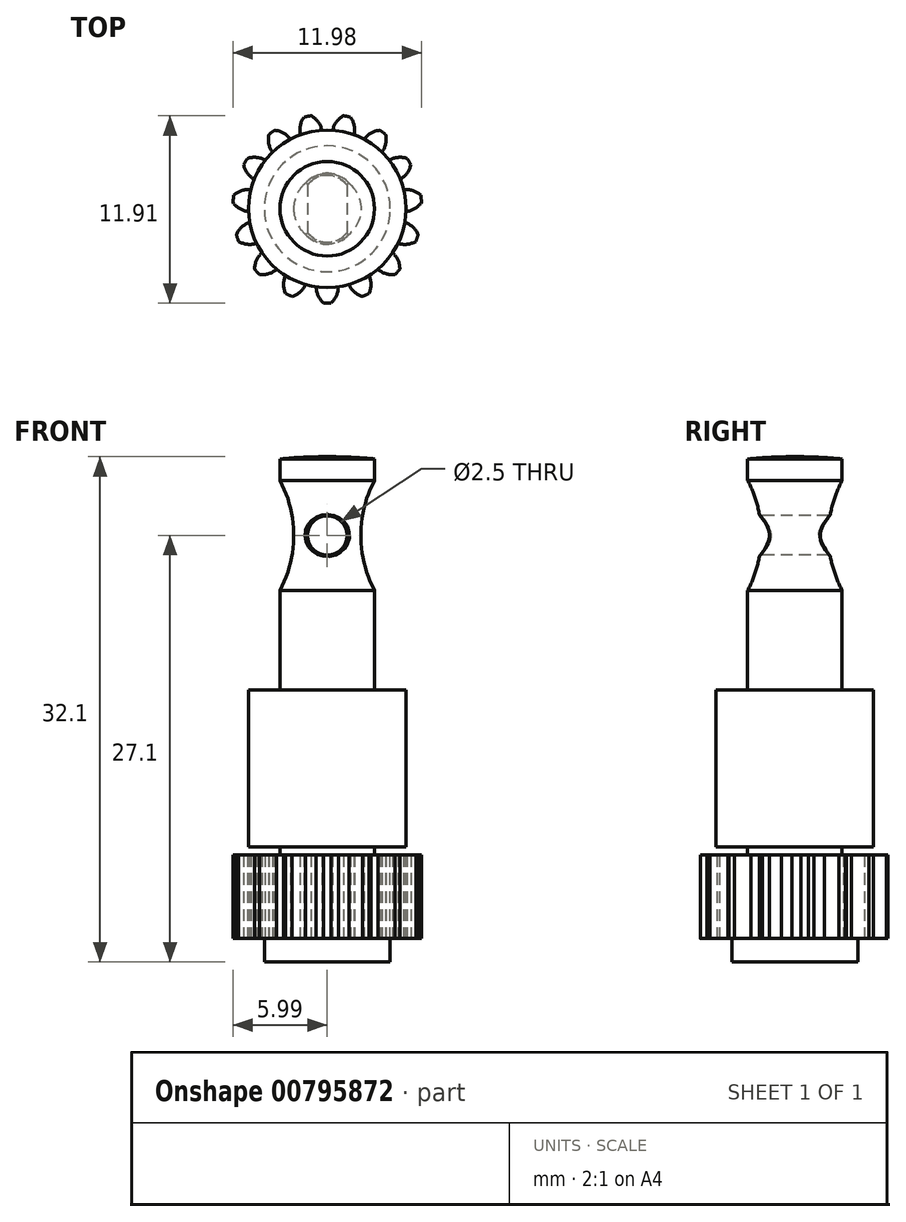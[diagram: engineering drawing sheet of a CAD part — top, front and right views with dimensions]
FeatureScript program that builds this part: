
annotation { "Feature Type Name" : "Feature", "Feature Type Description" : "" }
export const myFeature = defineFeature(function(context is Context, id is Id, definition is map)
    precondition{}
    {
        {
            assignVariable(context, id + "F0", {"name" : "H", "anyValue" : 24.8 + 7.3});
        }
        {
            var Q0;
            Q0=qCreatedBy(makeId("Top.planeOp"),FACE);
            var sketch = newSketch(context, id + "F1", { "sketchPlane" : qUnion([Q0])});
            skCircle(sketch, "E0", {"center": v(0, 0) * mm, "radius": 3 * mm});
            skSolve(sketch);
        }
        {
            var Q0;
            Q0=qSketchRegion(id+"F1",true);
            extrude(context, id + "F2", {"entities" : qUnion([Q0]), "depth" : (getVariable(context, 'H')) * mm, "offsetDistance" : 25 * mm});
        }
        {
            var Q0;
            Q0=makeQuery(id+"F2.opExtrude","CAP_FACE",FACE,{"disambiguationData":[OSD([sQuery(id+"F1.wireOp",EDGE,"E0")])],"isStart":true});
            var sketch = newSketch(context, id + "F3", { "sketchPlane" : qUnion([Q0])});
            skCircle(sketch, "E1", {"center": v(0, 0) * mm, "radius": 5 * mm});
            skCircle(sketch, "E2", {"center": v(0, 0) * mm, "radius": 3 * mm});
            skSolve(sketch);
        }
        {
            var Q0;
            Q0=qSketchRegion(id+"F3",true);
            extrude(context, id + "F4", {"entities" : qUnion([Q0]), "operationType" : NewBodyOperationType.ADD, "oppositeDirection" : true, "depth" : (getVariable(context, 'H') - 14.8) * mm, "offsetDistance" : 25 * mm, "hasSecondDirection" : true, "secondDirectionOppositeDirection" : true, "secondDirectionDepth" : 7.3 * mm});
        }
        {
            var Q0;
            Q0=makeQuery(id+"F4.boolean.opBoolean","MERGE",FACE,{"derivedFrom":[makeQuery(id+"F2.opExtrude","CAP_FACE",FACE,{"disambiguationData":[OSD([sQuery(id+"F1.wireOp",EDGE,"E0")])],"isStart":true}),makeQuery(id+"F4.opExtrude","CAP_FACE",FACE,{"disambiguationData":[OSD([sQuery(id+"F3.wireOp",EDGE,"E1")])],"isStart":true})]});
            var sketch = newSketch(context, id + "F5", { "sketchPlane" : qUnion([Q0])});
            skArc(sketch, "E3", {"start": v(-0.23, 6) * mm, "mid": v(0, 6) * mm, "end": v(0.23, 6) * mm});
            skArc(sketch, "E4", {"start": v(-0.7, 4.95) * mm, "mid": v(0, 5) * mm, "end": v(0.7, 4.95) * mm});
            skLineSegment(sketch, "E5", {"start": v(-0.7, 4.95) * mm, "end": v(0.7, 4.95) * mm, "construction": true});
            skLineSegment(sketch, "E6", {"start": v(0, 10.97) * mm, "end": v(0, 0) * mm, "construction": true});
            skArc(sketch, "E7", {"start": v(-0.7, 4.95) * mm, "mid": v(-0.58, 5.52) * mm, "end": v(-0.23, 6) * mm});
            skArc(sketch, "E8", {"start": v(0.7, 4.95) * mm, "mid": v(0.58, 5.52) * mm, "end": v(0.23, 6) * mm});
            skArc(sketch, "E9.1.0", {"start": v(-2.65, 5.38) * mm, "mid": v(-2.44, 5.48) * mm, "end": v(-2.23, 5.57) * mm});
            skArc(sketch, "E9.1.1", {"start": v(-2.65, 4.24) * mm, "mid": v(-2.77, 4.81) * mm, "end": v(-2.65, 5.38) * mm});
            skArc(sketch, "E9.1.2", {"start": v(-2.65, 4.24) * mm, "mid": v(-2.03, 4.57) * mm, "end": v(-1.37, 4.8) * mm});
            skLineSegment(sketch, "E9.1.3", {"start": v(-2.65, 4.24) * mm, "end": v(-1.37, 4.8) * mm, "construction": true});
            skArc(sketch, "E9.1.4", {"start": v(-1.37, 4.8) * mm, "mid": v(-1.72, 5.28) * mm, "end": v(-2.23, 5.57) * mm});
            skArc(sketch, "E9.2.0", {"start": v(-4.61, 3.84) * mm, "mid": v(-4.46, 4.01) * mm, "end": v(-4.3, 4.18) * mm});
            skArc(sketch, "E9.2.1", {"start": v(-4.15, 2.8) * mm, "mid": v(-4.5, 3.27) * mm, "end": v(-4.61, 3.84) * mm});
            skArc(sketch, "E9.2.2", {"start": v(-4.15, 2.8) * mm, "mid": v(-3.72, 3.35) * mm, "end": v(-3.21, 3.83) * mm});
            skLineSegment(sketch, "E9.2.3", {"start": v(-4.15, 2.8) * mm, "end": v(-3.21, 3.83) * mm, "construction": true});
            skArc(sketch, "E9.2.4", {"start": v(-3.21, 3.83) * mm, "mid": v(-3.72, 4.12) * mm, "end": v(-4.3, 4.18) * mm});
            skArc(sketch, "E10.4.3.0", {"start": v(-4.92, 0.86) * mm, "mid": v(-5.43, 1.16) * mm, "end": v(-5.77, 1.63) * mm});
            skArc(sketch, "E10.6.3.0", {"start": v(-5.77, 1.63) * mm, "mid": v(-5.7, 1.85) * mm, "end": v(-5.63, 2.07) * mm});
            skArc(sketch, "E10.8.3.0", {"start": v(-4.92, 0.86) * mm, "mid": v(-4.76, 1.55) * mm, "end": v(-4.5, 2.2) * mm});
            skLineSegment(sketch, "E10.12.3.0", {"start": v(-4.92, 0.86) * mm, "end": v(-4.5, 2.2) * mm, "construction": true});
            skArc(sketch, "E10.15.3.0", {"start": v(-4.5, 2.2) * mm, "mid": v(-5.07, 2.26) * mm, "end": v(-5.63, 2.07) * mm});
            skArc(sketch, "E10.4.4.0", {"start": v(-4.85, -1.21) * mm, "mid": v(-5.43, -1.15) * mm, "end": v(-5.94, -0.86) * mm});
            skArc(sketch, "E10.6.4.0", {"start": v(-5.94, -0.86) * mm, "mid": v(-5.97, -0.63) * mm, "end": v(-5.99, -0.4) * mm});
            skArc(sketch, "E10.8.4.0", {"start": v(-4.85, -1.21) * mm, "mid": v(-4.97, -0.52) * mm, "end": v(-5, 0.18) * mm});
            skLineSegment(sketch, "E10.12.4.0", {"start": v(-4.85, -1.21) * mm, "end": v(-5, 0.18) * mm, "construction": true});
            skArc(sketch, "E10.15.4.0", {"start": v(-5, 0.18) * mm, "mid": v(-5.55, 0) * mm, "end": v(-5.99, -0.4) * mm});
            skArc(sketch, "E10.4.5.0", {"start": v(-3.94, -3.08) * mm, "mid": v(-4.5, -3.26) * mm, "end": v(-5.08, -3.2) * mm});
            skArc(sketch, "E10.6.5.0", {"start": v(-5.08, -3.2) * mm, "mid": v(-5.2, -3) * mm, "end": v(-5.3, -2.8) * mm});
            skArc(sketch, "E10.8.5.0", {"start": v(-3.94, -3.08) * mm, "mid": v(-4.33, -2.5) * mm, "end": v(-4.64, -1.87) * mm});
            skLineSegment(sketch, "E10.12.5.0", {"start": v(-3.94, -3.08) * mm, "end": v(-4.64, -1.87) * mm, "construction": true});
            skArc(sketch, "E10.15.5.0", {"start": v(-4.64, -1.87) * mm, "mid": v(-5.07, -2.26) * mm, "end": v(-5.3, -2.8) * mm});
            skArc(sketch, "E10.4.6.0", {"start": v(-2.34, -4.42) * mm, "mid": v(-2.78, -4.8) * mm, "end": v(-3.34, -4.99) * mm});
            skArc(sketch, "E10.6.6.0", {"start": v(-3.34, -4.99) * mm, "mid": v(-3.53, -4.85) * mm, "end": v(-3.71, -4.71) * mm});
            skArc(sketch, "E10.8.6.0", {"start": v(-2.34, -4.42) * mm, "mid": v(-2.94, -4.05) * mm, "end": v(-3.48, -3.6) * mm});
            skLineSegment(sketch, "E10.12.6.0", {"start": v(-2.34, -4.42) * mm, "end": v(-3.48, -3.6) * mm, "construction": true});
            skArc(sketch, "E10.15.6.0", {"start": v(-3.48, -3.6) * mm, "mid": v(-3.71, -4.13) * mm, "end": v(-3.71, -4.71) * mm});
            skArc(sketch, "E10.4.7.0", {"start": v(-0.34, -4.99) * mm, "mid": v(-0.58, -5.52) * mm, "end": v(-1.02, -5.91) * mm});
            skArc(sketch, "E10.6.7.0", {"start": v(-1.02, -5.91) * mm, "mid": v(-1.25, -5.87) * mm, "end": v(-1.47, -5.82) * mm});
            skArc(sketch, "E10.8.7.0", {"start": v(-0.34, -4.99) * mm, "mid": v(-1.04, -4.9) * mm, "end": v(-1.71, -4.7) * mm});
            skLineSegment(sketch, "E10.12.7.0", {"start": v(-0.34, -4.99) * mm, "end": v(-1.71, -4.7) * mm, "construction": true});
            skArc(sketch, "E10.15.7.0", {"start": v(-1.71, -4.7) * mm, "mid": v(-1.71, -5.28) * mm, "end": v(-1.47, -5.82) * mm});
            skArc(sketch, "E10.4.8.0", {"start": v(1.71, -4.7) * mm, "mid": v(1.71, -5.28) * mm, "end": v(1.47, -5.82) * mm});
            skArc(sketch, "E10.6.8.0", {"start": v(1.47, -5.82) * mm, "mid": v(1.25, -5.87) * mm, "end": v(1.02, -5.91) * mm});
            skArc(sketch, "E10.8.8.0", {"start": v(1.71, -4.7) * mm, "mid": v(1.04, -4.9) * mm, "end": v(0.34, -4.99) * mm});
            skLineSegment(sketch, "E10.12.8.0", {"start": v(1.71, -4.7) * mm, "end": v(0.34, -4.99) * mm, "construction": true});
            skArc(sketch, "E10.15.8.0", {"start": v(0.34, -4.99) * mm, "mid": v(0.58, -5.52) * mm, "end": v(1.02, -5.91) * mm});
            skArc(sketch, "E10.4.9.0", {"start": v(3.48, -3.6) * mm, "mid": v(3.71, -4.13) * mm, "end": v(3.71, -4.71) * mm});
            skArc(sketch, "E10.6.9.0", {"start": v(3.71, -4.71) * mm, "mid": v(3.53, -4.85) * mm, "end": v(3.34, -4.99) * mm});
            skArc(sketch, "E10.8.9.0", {"start": v(3.48, -3.6) * mm, "mid": v(2.94, -4.05) * mm, "end": v(2.34, -4.42) * mm});
            skLineSegment(sketch, "E10.12.9.0", {"start": v(3.48, -3.6) * mm, "end": v(2.34, -4.42) * mm, "construction": true});
            skArc(sketch, "E10.15.9.0", {"start": v(2.34, -4.42) * mm, "mid": v(2.78, -4.8) * mm, "end": v(3.34, -4.99) * mm});
            skArc(sketch, "E10.4.10.0", {"start": v(4.64, -1.87) * mm, "mid": v(5.07, -2.26) * mm, "end": v(5.3, -2.8) * mm});
            skArc(sketch, "E10.6.10.0", {"start": v(5.3, -2.8) * mm, "mid": v(5.2, -3) * mm, "end": v(5.08, -3.2) * mm});
            skArc(sketch, "E10.8.10.0", {"start": v(4.64, -1.87) * mm, "mid": v(4.33, -2.5) * mm, "end": v(3.94, -3.08) * mm});
            skLineSegment(sketch, "E10.12.10.0", {"start": v(4.64, -1.87) * mm, "end": v(3.94, -3.08) * mm, "construction": true});
            skArc(sketch, "E10.15.10.0", {"start": v(3.94, -3.08) * mm, "mid": v(4.5, -3.26) * mm, "end": v(5.08, -3.2) * mm});
            skArc(sketch, "E10.4.11.0", {"start": v(5, 0.18) * mm, "mid": v(5.55, 0) * mm, "end": v(5.99, -0.4) * mm});
            skArc(sketch, "E10.6.11.0", {"start": v(5.99, -0.4) * mm, "mid": v(5.97, -0.63) * mm, "end": v(5.94, -0.86) * mm});
            skArc(sketch, "E10.8.11.0", {"start": v(5, 0.18) * mm, "mid": v(4.97, -0.52) * mm, "end": v(4.85, -1.21) * mm});
            skLineSegment(sketch, "E10.12.11.0", {"start": v(5, 0.18) * mm, "end": v(4.85, -1.21) * mm, "construction": true});
            skArc(sketch, "E10.15.11.0", {"start": v(4.85, -1.21) * mm, "mid": v(5.43, -1.15) * mm, "end": v(5.94, -0.86) * mm});
            skArc(sketch, "E11.4.12.0", {"start": v(4.5, 2.2) * mm, "mid": v(5.07, 2.26) * mm, "end": v(5.63, 2.07) * mm});
            skArc(sketch, "E11.6.12.0", {"start": v(5.63, 2.07) * mm, "mid": v(5.7, 1.85) * mm, "end": v(5.77, 1.63) * mm});
            skArc(sketch, "E11.8.12.0", {"start": v(4.5, 2.2) * mm, "mid": v(4.76, 1.55) * mm, "end": v(4.92, 0.86) * mm});
            skLineSegment(sketch, "E11.12.12.0", {"start": v(4.5, 2.2) * mm, "end": v(4.92, 0.86) * mm, "construction": true});
            skArc(sketch, "E11.15.12.0", {"start": v(4.92, 0.86) * mm, "mid": v(5.43, 1.16) * mm, "end": v(5.77, 1.63) * mm});
            skArc(sketch, "E11.4.13.0", {"start": v(3.21, 3.83) * mm, "mid": v(3.72, 4.12) * mm, "end": v(4.3, 4.18) * mm});
            skArc(sketch, "E11.6.13.0", {"start": v(4.3, 4.18) * mm, "mid": v(4.46, 4.01) * mm, "end": v(4.61, 3.84) * mm});
            skArc(sketch, "E11.8.13.0", {"start": v(3.21, 3.83) * mm, "mid": v(3.72, 3.35) * mm, "end": v(4.15, 2.8) * mm});
            skLineSegment(sketch, "E11.12.13.0", {"start": v(3.21, 3.83) * mm, "end": v(4.15, 2.8) * mm, "construction": true});
            skArc(sketch, "E11.15.13.0", {"start": v(4.15, 2.8) * mm, "mid": v(4.5, 3.27) * mm, "end": v(4.61, 3.84) * mm});
            skArc(sketch, "E12.4.14.0", {"start": v(1.37, 4.8) * mm, "mid": v(1.72, 5.28) * mm, "end": v(2.23, 5.57) * mm});
            skArc(sketch, "E12.6.14.0", {"start": v(2.23, 5.57) * mm, "mid": v(2.44, 5.48) * mm, "end": v(2.65, 5.38) * mm});
            skArc(sketch, "E12.8.14.0", {"start": v(1.37, 4.8) * mm, "mid": v(2.03, 4.57) * mm, "end": v(2.65, 4.24) * mm});
            skLineSegment(sketch, "E12.12.14.0", {"start": v(1.37, 4.8) * mm, "end": v(2.65, 4.24) * mm, "construction": true});
            skArc(sketch, "E12.15.14.0", {"start": v(2.65, 4.24) * mm, "mid": v(2.77, 4.81) * mm, "end": v(2.65, 5.38) * mm});
            skCircle(sketch, "E13", {"center": v(0, 0) * mm, "radius": 5 * mm});
            skSolve(sketch);
        }
        {
            var Q0;
            Q0=qSketchRegion(id+"F5",true);
            extrude(context, id + "F6", {"entities" : qUnion([Q0]), "operationType" : NewBodyOperationType.ADD, "oppositeDirection" : true, "depth" : 6.8 * mm, "offsetDistance" : 25 * mm});
        }
        {
            var Q0;
            Q0=qCreatedBy(makeId("Front.planeOp"),FACE);
            var sketch = newSketch(context, id + "F7", { "sketchPlane" : qUnion([Q0])});
            skLineSegment(sketch, "E14", {"start": v(0, 40.6) * mm, "end": v(0, -13.25) * mm, "construction": true});
            skArc(sketch, "E15", {"start": v(0, 32.1) * mm, "mid": v(5.06, 31.7) * mm, "end": v(10, 30.5) * mm});
            skLineSegment(sketch, "E16", {"start": v(0, 32.1) * mm, "end": v(0, 35.1) * mm});
            skLineSegment(sketch, "E17", {"start": v(0, 35.1) * mm, "end": v(10, 35.1) * mm});
            skLineSegment(sketch, "E18", {"start": v(10, 35.1) * mm, "end": v(10, 30.5) * mm});
            skSolve(sketch);
        }
        {
            var Q0;
            Q0=qSketchRegion(id+"F7",true);
            var Q1;
            Q1=sQuery(id+"F7.wireOp",EDGE,"E14");
            revolve(context, id + "F8", {"operationType" : NewBodyOperationType.REMOVE, "surfaceOperationType" : NewSurfaceOperationType.NEW, "entities" : qUnion([Q0]), "axis" : qUnion([Q1]), "revolveType" : RevolveType.FULL, "oppositeDirection" : true});
        }
        {
            var Q0;
            Q0=qCreatedBy(makeId("Front.planeOp"),FACE);
            var sketch = newSketch(context, id + "F9", { "sketchPlane" : qUnion([Q0])});
            skArc(sketch, "E19", {"start": v(3, 30.6) * mm, "mid": v(2.13, 27.1) * mm, "end": v(3, 23.6) * mm});
            skLineSegment(sketch, "E20", {"start": v(3, 30.6) * mm, "end": v(0, 30.6) * mm, "construction": true});
            skLineSegment(sketch, "E21", {"start": v(3, 23.6) * mm, "end": v(0, 23.6) * mm, "construction": true});
            skLineSegment(sketch, "E22", {"start": v(3, 0) * mm, "end": v(3, 30.6) * mm, "construction": true});
            skLineSegment(sketch, "E23", {"start": v(0, 30.6) * mm, "end": v(0, 23.6) * mm, "construction": true});
            skLineSegment(sketch, "E24", {"start": v(3, 30.6) * mm, "end": v(4.5, 30.6) * mm});
            skLineSegment(sketch, "E25", {"start": v(3, 23.6) * mm, "end": v(4.5, 23.6) * mm});
            skLineSegment(sketch, "E26", {"start": v(4.5, 23.6) * mm, "end": v(4.5, 30.6) * mm});
            skSolve(sketch);
        }
        {
            var Q0;
            Q0=qSketchRegion(id+"F9",true);
            var Q1;
            Q1=sQuery(id+"F9.wireOp",EDGE,"E23");
            revolve(context, id + "F10", {"operationType" : NewBodyOperationType.REMOVE, "surfaceOperationType" : NewSurfaceOperationType.NEW, "entities" : qUnion([Q0]), "axis" : qUnion([Q1]), "revolveType" : RevolveType.FULL, "oppositeDirection" : true});
        }
        {
            var Q0;
            Q0=qCreatedBy(makeId("Front.planeOp"),FACE);
            var sketch = newSketch(context, id + "F11", { "sketchPlane" : qUnion([Q0])});
            skCircle(sketch, "E27", {"center": v(0, 27.1) * mm, "radius": 1.25 * mm});
            skLineSegment(sketch, "E28", {"start": v(9.63, 27.1) * mm, "end": v(0, 27.1) * mm, "construction": true});
            skSolve(sketch);
        }
        {
            var Q0;
            Q0=qSketchRegion(id+"F11",true);
            extrude(context, id + "F12", {"entities" : qUnion([Q0]), "operationType" : NewBodyOperationType.REMOVE, "endBound" : BoundingType.SYMMETRIC, "oppositeDirection" : true, "depth" : 10 * mm, "offsetDistance" : 25 * mm});
        }
        {
            var Q0;
            Q0=makeQuery(id+"F12.boolean.opBoolean","INTERSECT",EDGE,{"disambiguationData":[OD(0.0)],"derivedFrom":[makeQuery(id+"F10.boolean.opBoolean","COPY",FACE,{"derivedFrom":makeQuery(id+"F10.opRevolve","SWEPT_FACE",FACE,{"disambiguationData":[OSD([sQuery(id+"F9.wireOp",EDGE,"E19")])]})}),makeQuery(id+"F12.opExtrude","SWEPT_FACE",FACE,{"disambiguationData":[OSD([sQuery(id+"F11.wireOp",EDGE,"E27")])]})]});
            fillet(context, id + "F13", {"entities" : qUnion([Q0]), "radius" : 0.1 * mm, "tangentPropagation" : true, "allowEdgeOverflow" : false});
        }
        {
            var Q0;
            Q0=makeQuery(id+"F12.boolean.opBoolean","INTERSECT",EDGE,{"disambiguationData":[OD(1.0)],"derivedFrom":[makeQuery(id+"F10.boolean.opBoolean","COPY",FACE,{"derivedFrom":makeQuery(id+"F10.opRevolve","SWEPT_FACE",FACE,{"disambiguationData":[OSD([sQuery(id+"F9.wireOp",EDGE,"E19")])]})}),makeQuery(id+"F12.opExtrude","SWEPT_FACE",FACE,{"disambiguationData":[OSD([sQuery(id+"F11.wireOp",EDGE,"E27")])]})]});
            fillet(context, id + "F14", {"entities" : qUnion([Q0]), "radius" : 0.1 * mm, "tangentPropagation" : true, "allowEdgeOverflow" : false});
        }
        {
            var Q0;
            Q0=qCreatedBy(makeId("Front.planeOp"),FACE);
            var sketch = newSketch(context, id + "F15", { "sketchPlane" : qUnion([Q0])});
            skLineSegment(sketch, "E29", {"start": v(0, -2) * mm, "end": v(0, 8.65) * mm, "construction": true});
            skLineSegment(sketch, "E30.bottom", {"start": v(6.5, 0) * mm, "end": v(4, 0) * mm});
            skLineSegment(sketch, "E30.top", {"start": v(6.5, 1.5) * mm, "end": v(4, 1.5) * mm});
            skLineSegment(sketch, "E30.left", {"start": v(6.5, 0) * mm, "end": v(6.5, 1.5) * mm});
            skLineSegment(sketch, "E30.right", {"start": v(4, 0) * mm, "end": v(4, 1.5) * mm});
            skLineSegment(sketch, "E31", {"start": v(4, 1.5) * mm, "end": v(0, 1.5) * mm});
            skSolve(sketch);
        }
        {
            var Q0;
            Q0=qSketchRegion(id+"F15",true);
            var Q1;
            Q1=sQuery(id+"F15.wireOp",EDGE,"E29");
            revolve(context, id + "F16", {"operationType" : NewBodyOperationType.REMOVE, "surfaceOperationType" : NewSurfaceOperationType.NEW, "entities" : qUnion([Q0]), "axis" : qUnion([Q1]), "revolveType" : RevolveType.FULL, "oppositeDirection" : true});
        }
    });
